# Revit family: KingswayGroup_SpprtRls_Anti-LigatureDropRailWallMounted
name_source: partatom
category: Specialty Equipment
units: mm (PartAtom-declared; Revit-internal decimal feet)

## family parameters
Always vertical = Yes
Cut with Voids When Loaded = No
Part Type = Normal
Room Calculation Point = No
Round Connector Dimension = Use Diameter
Shared = No
Work Plane-Based = No

## types (1)
- KingswayGroup_SpprtRls_Anti-LigatureDropRailWallMounted
    AssetType = Fixed
    BIMObjectName = KingswayGroup_SupportRails_Anti-LigatureDropRailWallMounted
    Category = Pr_40_20_76_84:Support rails
    Color = For full range of available finishes and colours, contact Kingsway Group
    Default Elevation = 0 mm  [stored 0 ft]
    Description = Drop Rail Support
    DurationUnit = year
    Features = Rated to 300kg, the KG255 is a high-strength drop rail designed to support service users in mental health ensuites and washroom facilities. The sturdy hinged rail can be safely locked in the upright position when not in use to ensure the ligature risk is minimised, while staff can unlock the unit and lower the rail when a service user requires support.
    Finish = For full range of available finishes and colours, contact Kingsway Group
    IfcExportAs = IfcRailingType
    IfcExportType = HANDRAIL
    Manufacturer = Kingsway Group
    ManufacturerName = Kingsway Group
    ManufacturerURL = https://kingswaygroupglobal.com
    Material = Heavy Gauge Steel
    Model = KG255
    ModelNumber = KG255
    ModelReference = Anti-Ligature Drop Rail Wall Mounted
    Name = SupportRails_Anti-LigatureDropRailWallMountedl_KG255_KingswayGroup
    NominalHeight = 993 mm  [stored 3.25787 ft]
    NominalLength = 807 mm
    NominalWidth = 100 mm  [stored 0.328084 ft]
    ProductInformation = https://kingswaygroupglobal.com
    RailsMaterial = NBS_Concept
    Size = 807 x 993 x 100 mm
    URL = https://kingswaygroupglobal.com
    Uniclass2015Code = Pr_40_20_76_84
    Uniclass2015Title = Support rails
    Uniclass2015Version = Products v1.36
    Version = 1
    WarrantyDescription = 5-Year Guarantee *For faulty manufacture and not for damage
    WarrantyDurationParts = 5
    WarrantyDurationUnit = year

note: [stored X ft] marks values corroborated as IEEE doubles in the binary element streams (Revit-internal decimal feet)

## geometry (parser evidence)
native form markers: Sweep x2
no freeform markers — native parametric forms only
